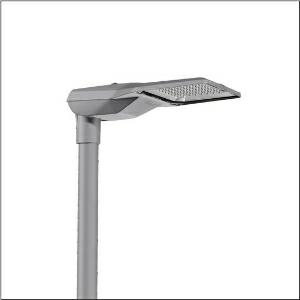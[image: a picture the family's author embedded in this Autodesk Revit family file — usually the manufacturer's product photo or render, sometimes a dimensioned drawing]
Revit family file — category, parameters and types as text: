
# Revit family: streetlight_sl_21_midi___st1_5a_5xe3p33s08lb_eae5
name_source: partatom
category: Lighting Fixtures
units: mm (PartAtom-declared; Revit-internal decimal feet)

## family parameters
Cut with Voids When Loaded = No
Host = Face
Light Source = No
Part Type = Normal
Room Calculation Point = No
Round Connector Dimension = Use Diameter
Shared = No

## types (1)
- --- (1 x LED, 14100 lm, 99.6 W, 3000K)
    Apparent Load = 100 VA
    CIE Flux Codes = 22 53 95 100 100
    Color Rendering = 70
    Color Temperature = 3000K
    Default Elevation = 1800 mm
    Description = Streetlight SL 21 midi, mast luminaire, primary light control with lens, of PMMA, primary optical cover: cover, of toughened safety glass, transparent, light distribution: ST1.5a, light emission: direct distribution, primary light characteristic: asymmetric, installation type: side-entry, post-top, LED, High Power LED, rated luminous flux: 14.100lm, luminous efficacy: 142lm/W, light colour: 730, colour temperature: 3000K, control gear: D4i, control: overheat protection, constant luminous flux control, time-dependent luminous flux control, flexible luminous flux parameterisation, pre-setting: logarithmic dimming characteristic, mains connection: 230..240V, AC, 50/60Hz, start of lifetime: 100W, end of service life: 102W, reduction: 46W, luminaire housing, of diecast aluminium, powder-coated, Siteco® metallic grey (DB 702S), corrosivity category C5 mid according to DIN EN ISO 12944, please order mast flange separately, inclination adjustable: 0°, 5°, 10°, 15°, sealing non-destructively replaceable, multi-level sealing system, length: 644mm, width: 335mm, height: 110mm, mast flange for spigot size: 42mm (side-entry): 5XC10008XM4, 60/48mm (side-entry/post-top): 5XC10108XM2, 76/60mm (side-entry/post-top): 5XC10108XM1, mounting height: 4..8m, Smart Interface above, protection rating (complete): IP66, insulation class (complete): insulation class II (safety insulation), certification: CE, ENEC, ENEC+, VDE, impact resistance: IK10, permissible operating ambient temperature for outdoor applications: -40..+50°C, standard-compliant lighting for roads and squares, packaging unit: 1 piece

Light Distribution: ST1.5a
    Height = 111 mm
    Lamp = 1 x LED
    Lamp Light Flux = 14100 lm
    Lamp Power = 99.6 W
    Lamp count = 1
    Length = 644 mm
    Luminous efficacy = 142 lm/W
    Manufacturer = Siteco
    ModVariant = No
    Model = 5XE3P33S08LB
    Number of Poles = 1
    OnlyDefault = Yes
    Power Factor = 1
    Product Name = Streetlight SL 21 midi | ST1.5a
    Product group = mast luminaire | pylon top
    ProductGroupID = 6100
    Protection Class = Protection class II
    Protection Degree = IP 66
    RLX_Detail_Level = 1
    RLX_Emergency_Light_Flux = 0 lm
    RLX_Emergency_Type = 0
    RLX_Emergency_Type_DB = No
    RlxData = <blob elided: 30313 chars, md5=284020e4>
    Socket = socket
    Standby Power = 0 W
    System Light Flux = 14100 lm
    System Power = 100 W
    Type Comments = factory setting: luminous flux: 100 % | dim-lin: 254 | 1020 mA
    Type Image = l_1004302.jpg
    URL = http://relux.com
    VarID = @adj_032771
    Voltage = 0 V
    Weight = 0.00 kg
    Width = 336 mm

## geometry (parser evidence)
native form markers: Blend x4, Sweep x11
no freeform markers — native parametric forms only
